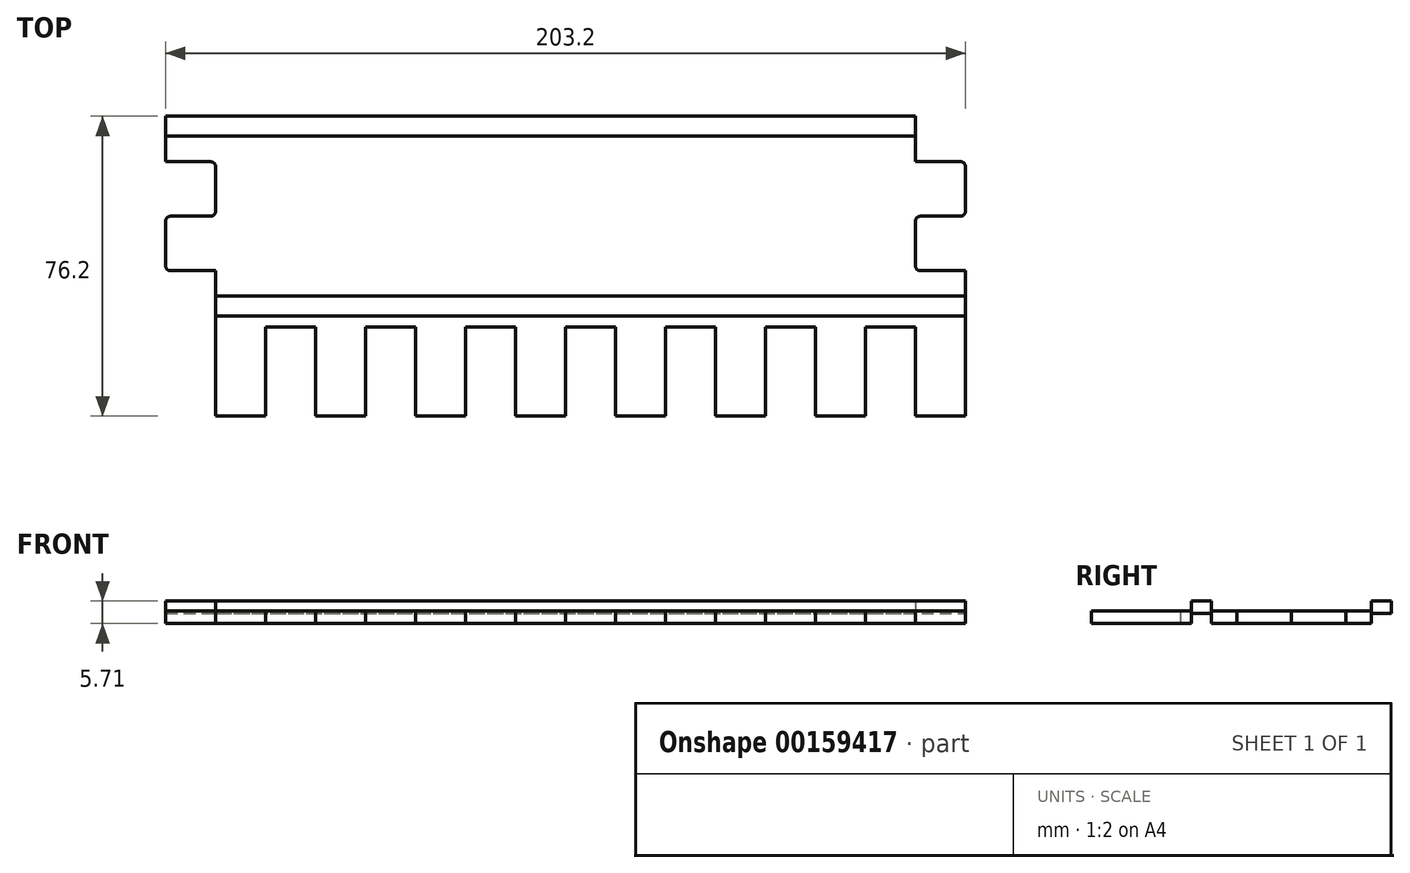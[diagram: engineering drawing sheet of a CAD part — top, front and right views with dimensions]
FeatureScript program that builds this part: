
annotation { "Feature Type Name" : "Feature", "Feature Type Description" : "" }
export const myFeature = defineFeature(function(context is Context, id is Id, definition is map)
    precondition{}
    {
        {
            var Q0;
            Q0=qCreatedBy(makeId("Top.planeOp"),FACE);
            var sketch = newSketch(context, id + "F0", { "sketchPlane" : qUnion([Q0])});
            skLineSegment(sketch, "E0.bottom", {"start": v(-40.87, 28.52) * mm, "end": v(149.63, 28.52) * mm});
            skLineSegment(sketch, "E0.right", {"start": v(162.33, -10.74) * mm, "end": v(162.33, -22.28) * mm});
            skLineSegment(sketch, "E1.0", {"start": v(-40.87, 23.44) * mm, "end": v(149.63, 23.44) * mm});
            skLineSegment(sketch, "E2.0", {"start": v(-28.17, -17.2) * mm, "end": v(162.33, -17.2) * mm});
            skLineSegment(sketch, "E3", {"start": v(162.33, -22.28) * mm, "end": v(162.33, -10.74) * mm});
            skLineSegment(sketch, "E4", {"start": v(162.33, -22.28) * mm, "end": v(149.63, -22.28) * mm});
            skLineSegment(sketch, "E5", {"start": v(149.63, -22.28) * mm, "end": v(136.93, -22.28) * mm});
            skLineSegment(sketch, "E6", {"start": v(136.93, -22.28) * mm, "end": v(124.23, -22.28) * mm});
            skLineSegment(sketch, "E7", {"start": v(124.23, -22.28) * mm, "end": v(111.53, -22.28) * mm});
            skLineSegment(sketch, "E8", {"start": v(111.53, -22.28) * mm, "end": v(98.83, -22.28) * mm});
            skLineSegment(sketch, "E9", {"start": v(98.83, -22.28) * mm, "end": v(86.13, -22.28) * mm});
            skLineSegment(sketch, "E10", {"start": v(86.13, -22.28) * mm, "end": v(73.43, -22.28) * mm});
            skLineSegment(sketch, "E11", {"start": v(73.43, -22.28) * mm, "end": v(60.73, -22.28) * mm});
            skLineSegment(sketch, "E12", {"start": v(60.73, -22.28) * mm, "end": v(48.03, -22.28) * mm});
            skLineSegment(sketch, "E13", {"start": v(48.03, -22.28) * mm, "end": v(35.33, -22.28) * mm});
            skLineSegment(sketch, "E14", {"start": v(35.33, -22.28) * mm, "end": v(22.63, -22.28) * mm});
            skLineSegment(sketch, "E15", {"start": v(22.63, -22.28) * mm, "end": v(9.93, -22.28) * mm});
            skLineSegment(sketch, "E16", {"start": v(9.93, -22.28) * mm, "end": v(-2.77, -22.28) * mm});
            skLineSegment(sketch, "E17", {"start": v(-2.77, -22.28) * mm, "end": v(-15.47, -22.28) * mm});
            skLineSegment(sketch, "E18", {"start": v(-15.47, -22.28) * mm, "end": v(-28.17, -22.28) * mm});
            skLineSegment(sketch, "E19.MirrorCS", {"start": v(-15.47, 28.52) * mm, "end": v(-28.17, 28.52) * mm});
            skLineSegment(sketch, "E20.MirrorCS", {"start": v(9.93, 28.52) * mm, "end": v(-2.77, 28.52) * mm});
            skLineSegment(sketch, "E21.MirrorCS", {"start": v(35.33, 28.52) * mm, "end": v(22.63, 28.52) * mm});
            skLineSegment(sketch, "E22.MirrorCS", {"start": v(86.13, 28.52) * mm, "end": v(73.43, 28.52) * mm});
            skLineSegment(sketch, "E23.MirrorCS", {"start": v(73.43, 28.52) * mm, "end": v(60.73, 28.52) * mm});
            skLineSegment(sketch, "E24.MirrorCS", {"start": v(60.73, 28.52) * mm, "end": v(48.03, 28.52) * mm});
            skLineSegment(sketch, "E25.MirrorCS", {"start": v(149.63, 28.52) * mm, "end": v(136.93, 28.52) * mm});
            skLineSegment(sketch, "E26.MirrorCS", {"start": v(136.93, 28.52) * mm, "end": v(124.23, 28.52) * mm});
            skLineSegment(sketch, "E27.MirrorCS", {"start": v(124.23, 28.52) * mm, "end": v(111.53, 28.52) * mm});
            skLineSegment(sketch, "E28.MirrorCS", {"start": v(111.53, 28.52) * mm, "end": v(98.83, 28.52) * mm});
            skLineSegment(sketch, "E29.MirrorCS", {"start": v(48.03, 28.52) * mm, "end": v(35.33, 28.52) * mm});
            skLineSegment(sketch, "E30.MirrorCS", {"start": v(98.83, 28.52) * mm, "end": v(86.13, 28.52) * mm});
            skLineSegment(sketch, "E31.MirrorCS", {"start": v(22.63, 28.52) * mm, "end": v(9.93, 28.52) * mm});
            skLineSegment(sketch, "E32.MirrorCS", {"start": v(-28.17, 28.52) * mm, "end": v(-40.87, 28.52) * mm});
            skLineSegment(sketch, "E33.MirrorCS", {"start": v(-2.77, 28.52) * mm, "end": v(-15.47, 28.52) * mm});
            skLineSegment(sketch, "E34", {"start": v(162.33, -22.28) * mm, "end": v(162.33, -47.68) * mm});
            skLineSegment(sketch, "E35", {"start": v(162.33, -47.68) * mm, "end": v(149.63, -47.68) * mm});
            skLineSegment(sketch, "E36", {"start": v(149.63, -47.68) * mm, "end": v(149.63, -25.07) * mm});
            skLineSegment(sketch, "E37", {"start": v(136.93, -25.07) * mm, "end": v(136.93, -47.68) * mm});
            skLineSegment(sketch, "E38", {"start": v(136.93, -47.68) * mm, "end": v(124.23, -47.68) * mm});
            skLineSegment(sketch, "E39", {"start": v(124.23, -47.68) * mm, "end": v(124.23, -25.07) * mm});
            skLineSegment(sketch, "E40", {"start": v(124.23, -25.07) * mm, "end": v(111.53, -25.07) * mm});
            skLineSegment(sketch, "E41", {"start": v(111.53, -25.07) * mm, "end": v(111.53, -47.68) * mm});
            skLineSegment(sketch, "E42", {"start": v(111.53, -47.68) * mm, "end": v(98.83, -47.68) * mm});
            skLineSegment(sketch, "E43", {"start": v(98.83, -47.68) * mm, "end": v(98.83, -25.07) * mm});
            skLineSegment(sketch, "E44", {"start": v(98.83, -25.07) * mm, "end": v(86.13, -25.07) * mm});
            skLineSegment(sketch, "E45", {"start": v(86.13, -25.07) * mm, "end": v(86.13, -47.68) * mm});
            skLineSegment(sketch, "E46", {"start": v(86.13, -47.68) * mm, "end": v(73.43, -47.68) * mm});
            skLineSegment(sketch, "E47", {"start": v(73.43, -47.68) * mm, "end": v(73.43, -25.07) * mm});
            skLineSegment(sketch, "E48", {"start": v(73.43, -25.07) * mm, "end": v(60.73, -25.07) * mm});
            skLineSegment(sketch, "E49", {"start": v(60.73, -25.07) * mm, "end": v(60.73, -47.68) * mm});
            skLineSegment(sketch, "E50", {"start": v(60.73, -47.68) * mm, "end": v(48.03, -47.68) * mm});
            skLineSegment(sketch, "E51", {"start": v(48.03, -47.68) * mm, "end": v(48.03, -25.07) * mm});
            skLineSegment(sketch, "E52", {"start": v(48.03, -25.07) * mm, "end": v(35.33, -25.07) * mm});
            skLineSegment(sketch, "E53", {"start": v(35.33, -25.07) * mm, "end": v(35.33, -47.68) * mm});
            skLineSegment(sketch, "E54", {"start": v(35.33, -47.68) * mm, "end": v(22.63, -47.68) * mm});
            skLineSegment(sketch, "E55", {"start": v(22.63, -47.68) * mm, "end": v(22.63, -25.07) * mm});
            skLineSegment(sketch, "E56", {"start": v(22.63, -25.07) * mm, "end": v(9.93, -25.07) * mm});
            skLineSegment(sketch, "E57", {"start": v(9.93, -25.07) * mm, "end": v(9.93, -47.68) * mm});
            skLineSegment(sketch, "E58", {"start": v(9.93, -47.68) * mm, "end": v(-2.77, -47.68) * mm});
            skLineSegment(sketch, "E59", {"start": v(-2.77, -47.68) * mm, "end": v(-2.77, -25.07) * mm});
            skLineSegment(sketch, "E60", {"start": v(-2.77, -25.07) * mm, "end": v(-15.47, -25.07) * mm});
            skLineSegment(sketch, "E61", {"start": v(-15.47, -25.07) * mm, "end": v(-15.47, -47.68) * mm});
            skLineSegment(sketch, "E62", {"start": v(-15.47, -47.68) * mm, "end": v(-28.17, -47.68) * mm});
            skLineSegment(sketch, "E63", {"start": v(-28.17, -47.68) * mm, "end": v(-28.17, -25.07) * mm});
            skLineSegment(sketch, "E64", {"start": v(-28.17, -25.07) * mm, "end": v(-28.17, -22.28) * mm});
            skLineSegment(sketch, "E65", {"start": v(-40.87, 31.06) * mm, "end": v(-40.87, 16.96) * mm});
            skLineSegment(sketch, "E66", {"start": v(-28.17, -10.74) * mm, "end": v(-28.17, -22.28) * mm});
            skLineSegment(sketch, "E67", {"start": v(-28.17, -10.74) * mm, "end": v(-39.6, -10.74) * mm});
            skLineSegment(sketch, "E68", {"start": v(-39.6, 3.12) * mm, "end": v(-29.44, 3.12) * mm});
            skLineSegment(sketch, "E69", {"start": v(-28.17, 4.39) * mm, "end": v(-28.17, 15.7) * mm});
            skLineSegment(sketch, "E70", {"start": v(-29.44, 16.96) * mm, "end": v(-40.87, 16.96) * mm});
            skLineSegment(sketch, "E71.trimOffspring", {"start": v(-40.87, 1.85) * mm, "end": v(-40.87, -9.47) * mm});
            skPoint(sketch, "E72.visualSharp", {"position": v(-40.87, -10.74) * mm});
            skArc(sketch, "E72.filletArc", {"start": v(-40.87, -9.47) * mm, "mid": v(-40.5, -10.37) * mm, "end": v(-39.6, -10.74) * mm});
            skPoint(sketch, "E73.visualSharp", {"position": v(-40.87, 3.12) * mm});
            skArc(sketch, "E73.filletArc", {"start": v(-39.6, 3.12) * mm, "mid": v(-40.5, 2.75) * mm, "end": v(-40.87, 1.85) * mm});
            skPoint(sketch, "E74.visualSharp", {"position": v(-28.17, 3.12) * mm});
            skArc(sketch, "E74.filletArc", {"start": v(-29.44, 3.12) * mm, "mid": v(-28.54, 3.49) * mm, "end": v(-28.17, 4.39) * mm});
            skPoint(sketch, "E75.visualSharp", {"position": v(-28.17, 16.96) * mm});
            skArc(sketch, "E75.filletArc", {"start": v(-28.17, 15.7) * mm, "mid": v(-28.54, 16.59) * mm, "end": v(-29.44, 16.96) * mm});
            skLineSegment(sketch, "E76", {"start": v(-40.87, 28.52) * mm, "end": v(-40.87, 53.92) * mm});
            skLineSegment(sketch, "E77", {"start": v(-40.87, 53.92) * mm, "end": v(-28.17, 53.92) * mm});
            skLineSegment(sketch, "E78", {"start": v(-28.17, 53.92) * mm, "end": v(-28.17, 31.06) * mm});
            skLineSegment(sketch, "E79", {"start": v(-28.17, 31.06) * mm, "end": v(-15.47, 31.06) * mm});
            skLineSegment(sketch, "E80", {"start": v(-15.47, 31.06) * mm, "end": v(-15.47, 53.92) * mm});
            skLineSegment(sketch, "E81", {"start": v(-15.47, 53.92) * mm, "end": v(-2.77, 53.92) * mm});
            skLineSegment(sketch, "E82", {"start": v(-2.77, 53.92) * mm, "end": v(-2.77, 31.06) * mm});
            skLineSegment(sketch, "E83", {"start": v(-2.77, 31.06) * mm, "end": v(9.93, 31.06) * mm});
            skLineSegment(sketch, "E84", {"start": v(9.93, 31.06) * mm, "end": v(9.93, 53.92) * mm});
            skLineSegment(sketch, "E85", {"start": v(9.93, 53.92) * mm, "end": v(22.63, 53.92) * mm});
            skLineSegment(sketch, "E86", {"start": v(22.63, 53.92) * mm, "end": v(22.63, 31.06) * mm});
            skLineSegment(sketch, "E87", {"start": v(22.63, 31.06) * mm, "end": v(35.33, 31.06) * mm});
            skLineSegment(sketch, "E88", {"start": v(35.33, 31.06) * mm, "end": v(35.33, 53.92) * mm});
            skLineSegment(sketch, "E89", {"start": v(35.33, 53.92) * mm, "end": v(48.03, 53.92) * mm});
            skLineSegment(sketch, "E90", {"start": v(60.73, 53.92) * mm, "end": v(73.43, 53.92) * mm});
            skLineSegment(sketch, "E91", {"start": v(73.43, 53.92) * mm, "end": v(73.43, 31.06) * mm});
            skLineSegment(sketch, "E92", {"start": v(73.43, 31.06) * mm, "end": v(86.13, 31.06) * mm});
            skLineSegment(sketch, "E93", {"start": v(86.13, 31.06) * mm, "end": v(86.13, 53.92) * mm});
            skLineSegment(sketch, "E94", {"start": v(86.13, 53.92) * mm, "end": v(98.83, 53.92) * mm});
            skLineSegment(sketch, "E95", {"start": v(98.83, 53.92) * mm, "end": v(98.83, 31.06) * mm});
            skLineSegment(sketch, "E96", {"start": v(98.83, 31.06) * mm, "end": v(111.53, 31.06) * mm});
            skLineSegment(sketch, "E97", {"start": v(111.53, 31.06) * mm, "end": v(111.53, 53.92) * mm});
            skLineSegment(sketch, "E98", {"start": v(111.53, 53.92) * mm, "end": v(124.23, 53.92) * mm});
            skLineSegment(sketch, "E99", {"start": v(124.23, 53.92) * mm, "end": v(124.23, 31.06) * mm});
            skLineSegment(sketch, "E100", {"start": v(124.23, 31.06) * mm, "end": v(136.93, 31.06) * mm});
            skLineSegment(sketch, "E101", {"start": v(136.93, 31.06) * mm, "end": v(136.93, 53.92) * mm});
            skLineSegment(sketch, "E102", {"start": v(136.93, 53.92) * mm, "end": v(149.63, 53.92) * mm});
            skLineSegment(sketch, "E103", {"start": v(149.63, 53.92) * mm, "end": v(149.63, 31.06) * mm});
            skLineSegment(sketch, "E104", {"start": v(136.93, -25.07) * mm, "end": v(149.63, -25.07) * mm});
            skLineSegment(sketch, "E105", {"start": v(48.03, 53.92) * mm, "end": v(48.03, 31.06) * mm});
            skLineSegment(sketch, "E106", {"start": v(48.03, 31.06) * mm, "end": v(60.73, 31.06) * mm});
            skLineSegment(sketch, "E107", {"start": v(60.73, 31.06) * mm, "end": v(60.73, 53.92) * mm});
            skLineSegment(sketch, "E108", {"start": v(149.63, 31.06) * mm, "end": v(149.63, 28.52) * mm});
            skLineSegment(sketch, "E109", {"start": v(149.63, 28.52) * mm, "end": v(149.63, 16.97) * mm});
            skLineSegment(sketch, "E110", {"start": v(149.63, 16.97) * mm, "end": v(161.06, 16.97) * mm});
            skLineSegment(sketch, "E111", {"start": v(161.06, 3.12) * mm, "end": v(150.9, 3.12) * mm});
            skLineSegment(sketch, "E112", {"start": v(149.63, 1.85) * mm, "end": v(149.63, -9.47) * mm});
            skLineSegment(sketch, "E113", {"start": v(150.9, -10.74) * mm, "end": v(162.33, -10.74) * mm});
            skLineSegment(sketch, "E114.trimOffspring", {"start": v(162.33, 4.39) * mm, "end": v(162.33, 15.7) * mm});
            skPoint(sketch, "E115.visualSharp", {"position": v(162.33, 16.97) * mm});
            skArc(sketch, "E115.filletArc", {"start": v(162.33, 15.7) * mm, "mid": v(161.96, 16.6) * mm, "end": v(161.06, 16.97) * mm});
            skPoint(sketch, "E116.visualSharp", {"position": v(162.33, 3.12) * mm});
            skArc(sketch, "E116.filletArc", {"start": v(161.06, 3.12) * mm, "mid": v(161.96, 3.49) * mm, "end": v(162.33, 4.39) * mm});
            skPoint(sketch, "E117.visualSharp", {"position": v(149.63, 3.12) * mm});
            skArc(sketch, "E117.filletArc", {"start": v(150.9, 3.12) * mm, "mid": v(150, 2.75) * mm, "end": v(149.63, 1.85) * mm});
            skPoint(sketch, "E118.visualSharp", {"position": v(149.63, -10.74) * mm});
            skArc(sketch, "E118.filletArc", {"start": v(149.63, -9.47) * mm, "mid": v(150, -10.37) * mm, "end": v(150.9, -10.74) * mm});
            skSolve(sketch);
        }
        {
            var Q0;
            Q0=makeQuery(id+"F0.imprint","IMPRINT",FACE,{"disambiguationData":[TD([[makeQuery(id+"F0.imprint","IMPRINT",EDGE,{"derivedFrom":sQuery(id+"F0.wireOp",EDGE,"E4")}),1.0]])]});
            var Q1;
            Q1=makeQuery(id+"F0.imprint","IMPRINT",FACE,{"disambiguationData":[TD([[makeQuery(id+"F0.imprint","IMPRINT",EDGE,{"derivedFrom":sQuery(id+"F0.wireOp",EDGE,"E19.MirrorCS")}),-1.0]])]});
            var Q2;
            {var subQ1=sQuery(id+"F0.wireOp",EDGE,"E1.0");Q2=makeQuery(id+"F0.imprint","IMPRINT",FACE,{"disambiguationData":[TD([[makeQuery(id+"F0.imprint","IMPRINT",EDGE,{"derivedFrom":subQ1}),-1.0]])]});}
            extrude(context, id + "F1", {"entities" : qUnion([Q0, Q1, Q2]), "depth" : 3.17 * mm});
        }
        {
            var Q0;
            {var subQ2=sQuery(id+"F0.wireOp",EDGE,"E1.0");Q0=makeQuery(id+"F0.imprint","IMPRINT",FACE,{"disambiguationData":[TD([[makeQuery(id+"F0.imprint","IMPRINT",EDGE,{"derivedFrom":subQ2}),1.0]])]});}
            var Q1;
            {var subQ0=sQuery(id+"F0.wireOp",EDGE,"E2.0");Q1=makeQuery(id+"F0.imprint","IMPRINT",FACE,{"disambiguationData":[TD([[makeQuery(id+"F0.imprint","IMPRINT",EDGE,{"derivedFrom":subQ0}),-1.0]])]});}
            extrude(context, id + "F2", {"entities" : qUnion([Q0, Q1]), "depth" : 5.7 * mm});
        }
        {
            var Q0;
            {var subQ2=sQuery(id+"F0.wireOp",EDGE,"E1.0");Q0=makeQuery(id+"F0.imprint","IMPRINT",FACE,{"disambiguationData":[TD([[makeQuery(id+"F0.imprint","IMPRINT",EDGE,{"derivedFrom":subQ2}),1.0]])]});}
            var Q1;
            {var subQ0=sQuery(id+"F0.wireOp",EDGE,"E2.0");Q1=makeQuery(id+"F0.imprint","IMPRINT",FACE,{"disambiguationData":[TD([[makeQuery(id+"F0.imprint","IMPRINT",EDGE,{"derivedFrom":subQ0}),-1.0]])]});}
            extrude(context, id + "F3", {"entities" : qUnion([Q0, Q1]), "operationType" : NewBodyOperationType.REMOVE, "depth" : 2.54 * mm});
        }
    });
